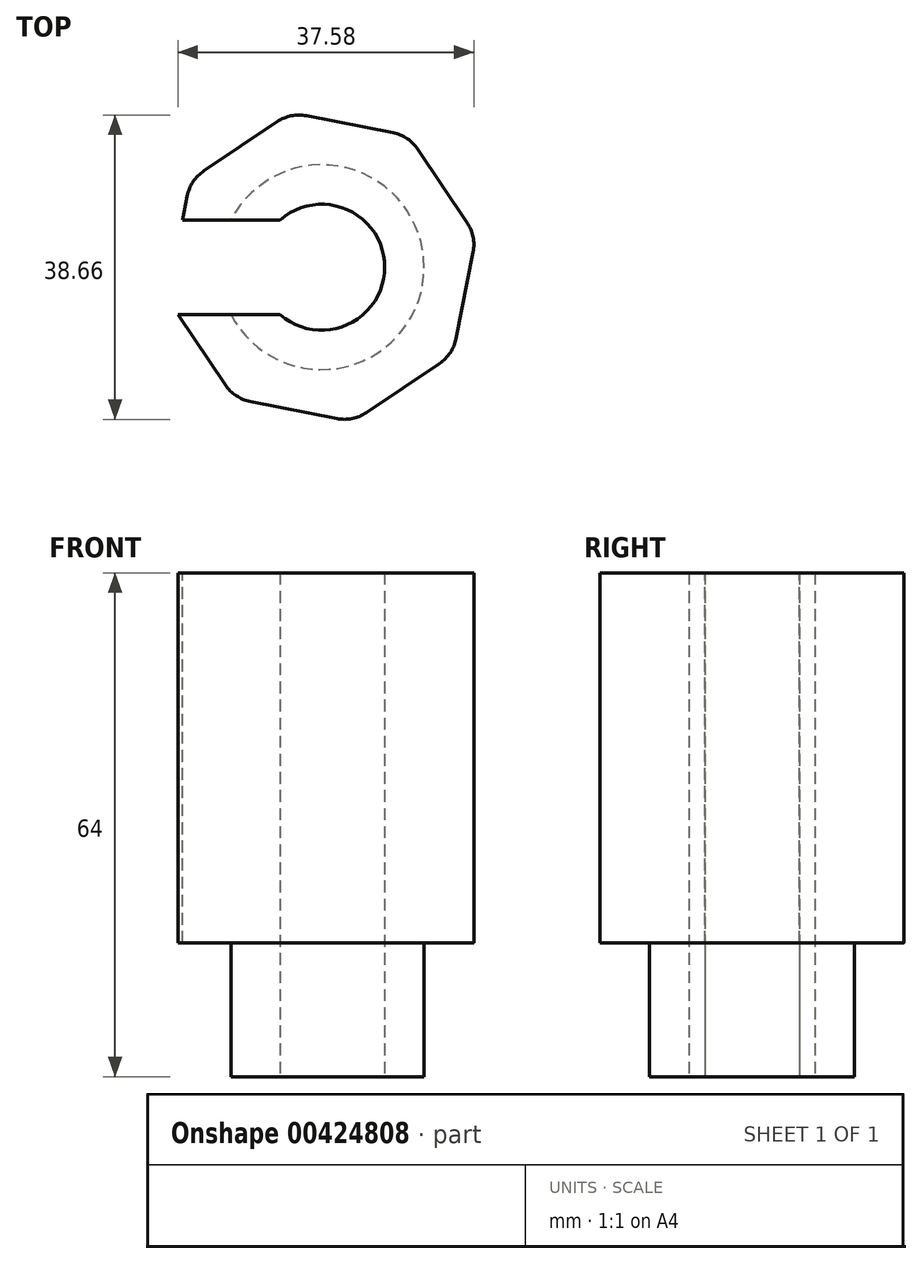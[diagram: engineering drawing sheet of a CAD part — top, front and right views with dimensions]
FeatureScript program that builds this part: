
annotation { "Feature Type Name" : "Feature", "Feature Type Description" : "" }
export const myFeature = defineFeature(function(context is Context, id is Id, definition is map)
    precondition{}
    {
        {
            var Q0;
            Q0=qCreatedBy(makeId("Top.planeOp"),FACE);
            var sketch = newSketch(context, id + "F0", { "sketchPlane" : qUnion([Q0])});
            skCircle(sketch, "E0", {"center": v(0, 0) * mm, "radius": 13 * mm});
            skCircle(sketch, "E1", {"center": v(0, 0) * mm, "radius": 8 * mm});
            skLineSegment(sketch, "E2", {"start": v(-9.15, -9.23) * mm, "end": v(0, 0) * mm});
            skLineSegment(sketch, "E3", {"start": v(0, 0) * mm, "end": v(9.15, 9.23) * mm});
            skLineSegment(sketch, "E4", {"start": v(0, 0) * mm, "end": v(-9.23, 9.15) * mm});
            skLineSegment(sketch, "E5.bottom", {"start": v(-9.15, -9.23) * mm, "end": v(9.15, -9.23) * mm});
            skLineSegment(sketch, "E5.top", {"start": v(-9.15, 9.15) * mm, "end": v(9.15, 9.15) * mm});
            skLineSegment(sketch, "E5.left", {"start": v(-9.15, -9.23) * mm, "end": v(-9.15, 9.15) * mm});
            skLineSegment(sketch, "E5.right", {"start": v(9.15, -9.23) * mm, "end": v(9.15, 9.15) * mm});
            skSolve(sketch);
        }
        {
            var Q0;
            {var subQ0=sQuery(id+"F0.wireOp",EDGE,"E5.bottom");Q0=makeQuery(id+"F0.imprint","IMPRINT",FACE,{"disambiguationData":[TD([[makeQuery(id+"F0.imprint","IMPRINT",EDGE,{"derivedFrom":subQ0}),-1.0]])]});}
            var Q1;
            {var subQ0=sQuery(id+"F0.wireOp",EDGE,"E5.bottom");Q1=makeQuery(id+"F0.imprint","IMPRINT",FACE,{"disambiguationData":[TD([[makeQuery(id+"F0.imprint","IMPRINT",EDGE,{"derivedFrom":subQ0}),1.0]])]});}
            var Q2;
            {var subQ0=sQuery(id+"F0.wireOp",EDGE,"E4");var subQ1=sQuery(id+"F0.wireOp",EDGE,"E1");var subQ2=makeQuery(id+"F0.imprint","INTERSECT",VERTEX,{"derivedFrom":[subQ1,subQ0]});Q2=makeQuery(id+"F0.imprint","IMPRINT",FACE,{"disambiguationData":[TD([[makeQuery(id+"F0.imprint","IMPRINT",EDGE,{"disambiguationData":[TD([[subQ2,-1.0]])],"derivedFrom":subQ1}),-1.0]])]});}
            var Q3;
            {var subQ5=sQuery(id+"F0.wireOp",EDGE,"E4");var subQ6=sQuery(id+"F0.wireOp",EDGE,"E1");var subQ7=makeQuery(id+"F0.imprint","INTERSECT",VERTEX,{"derivedFrom":[subQ6,subQ5]});Q3=makeQuery(id+"F0.imprint","IMPRINT",FACE,{"disambiguationData":[TD([[makeQuery(id+"F0.imprint","IMPRINT",EDGE,{"disambiguationData":[TD([[subQ7,1.0]])],"derivedFrom":subQ6}),-1.0]])]});}
            var Q4;
            {var subQ1=sQuery(id+"F0.wireOp",EDGE,"E0");var subQ7=sQuery(id+"F0.wireOp",EDGE,"E3");var subQ9=makeQuery(id+"F0.imprint","INTERSECT",VERTEX,{"derivedFrom":[subQ1,subQ7]});Q4=makeQuery(id+"F0.imprint","IMPRINT",FACE,{"disambiguationData":[TD([[makeQuery(id+"F0.imprint","IMPRINT",EDGE,{"disambiguationData":[TD([[subQ9,-1.0]])],"derivedFrom":subQ1}),1.0]])]});}
            extrude(context, id + "F1", {"entities" : qUnion([Q0, Q1, Q2, Q3, Q4]), "depth" : 24 * mm});
        }
        {
            var Q0;
            Q0 = qSketchRegion(id + "F0", true);
            var Q1;
            Q1=sQuery(id+"F0.wireOp",EDGE,"E0");
            var Q2;
            Q2=sQuery(id+"F0.wireOp",EDGE,"E1");
            extrude(context, id + "F2", {"entities" : qUnion([Q0]), "operationType" : NewBodyOperationType.ADD, "surfaceEntities" : qUnion([Q1, Q2]), "depth" : 17 * mm});
        }
        {
            var Q0;
            Q0=makeQuery(id+"F1.opExtrude","CAP_FACE",FACE,{"disambiguationData":[OSD([sQuery(id+"F0.wireOp",EDGE,"E0"),sQuery(id+"F0.wireOp",EDGE,"E1"),sQuery(id+"F0.wireOp",EDGE,"E3"),sQuery(id+"F0.wireOp",EDGE,"E4"),sQuery(id+"F0.wireOp",EDGE,"E5.top"),sQuery(id+"F0.wireOp",EDGE,"E5.left"),sQuery(id+"F0.wireOp",EDGE,"E5.right")])],"isStart":false});
            var sketch = newSketch(context, id + "F3", { "sketchPlane" : qUnion([Q0])});
            skLineSegment(sketch, "E6", {"start": v(-9.15, -9.23) * mm, "end": v(-9.15, 9.07) * mm});
            skLineSegment(sketch, "E7", {"start": v(9.15, -9.23) * mm, "end": v(9.15, 9.23) * mm});
            skArc(sketch, "E8", {"start": v(9.15, 9.23) * mm, "mid": v(-0.03, 12.94) * mm, "end": v(-9.15, 9.07) * mm});
            skArc(sketch, "E9", {"start": v(-9.15, -9.23) * mm, "mid": v(0, -13) * mm, "end": v(9.15, -9.23) * mm});
            skSolve(sketch);
        }
        {
            var Q0;
            Q0=makeQuery(id+"F3.imprint","IMPRINT",FACE,{"disambiguationData":[TD([[makeQuery(id+"F3.imprint","IMPRINT",EDGE,{"derivedFrom":sQuery(id+"F3.wireOp",EDGE,"E6")}),-1.0]])]});
            extrude(context, id + "F4", {"entities" : qUnion([Q0]), "depth" : 40 * mm});
        }
        {
            var Q0;
            {var subQ0=sQuery(id+"F0.wireOp",EDGE,"E4");var subQ1=sQuery(id+"F0.wireOp",EDGE,"E5.left");var subQ3=sQuery(id+"F0.wireOp",EDGE,"E0");var subQ4=sQuery(id+"F0.wireOp",EDGE,"E3");Q0=makeQuery(id+"F2.boolean.opBoolean","SPLIT",FACE,{"disambiguationData":[TD([makeQuery(id+"F1.opExtrude","SWEPT_FACE",FACE,{"disambiguationData":[OSD([subQ0])]})])],"derivedFrom":makeQuery(id+"F2.opExtrude","CAP_FACE",FACE,{"disambiguationData":[OSD([subQ3,sQuery(id+"F0.wireOp",EDGE,"E1"),subQ4,subQ0,sQuery(id+"F0.wireOp",EDGE,"E5.top"),subQ1])],"isStart":false})});}
            var sketch = newSketch(context, id + "F5", { "sketchPlane" : qUnion([Q0])});
            skSolve(sketch);
        }
        {
            var Q0;
            Q0 = qSketchRegion(id + "F5", true);
            var Q1;
            {var subQ0=sQuery(id+"F0.wireOp",EDGE,"E5.left");var subQ1=sQuery(id+"F0.wireOp",EDGE,"E4");var subQ2=sQuery(id+"F0.wireOp",EDGE,"E3");var subQ3=sQuery(id+"F0.wireOp",EDGE,"E0");var subQ4=makeQuery(id+"F2.opExtrude","CAP_FACE",FACE,{"disambiguationData":[OSD([subQ3,sQuery(id+"F0.wireOp",EDGE,"E1"),subQ2,subQ1,sQuery(id+"F0.wireOp",EDGE,"E5.top"),subQ0])],"isStart":false});var subQ5=makeQuery(id+"F1.opExtrude","SWEPT_FACE",FACE,{"disambiguationData":[OSD([subQ1])]});Q1=makeQuery(id+"F5.imprint","IMPRINT",FACE,{"disambiguationData":[TD([[makeQuery(id+"F5.imprint","IMPRINT",EDGE,{"derivedFrom":makeQuery(id+"F2.boolean.opBoolean","INTERSECT",EDGE,{"derivedFrom":[subQ5,subQ4]})}),1.0]])]});}
            extrude(context, id + "F6", {"entities" : qUnion([Q0, Q1]), "operationType" : NewBodyOperationType.ADD, "depth" : 47 * mm});
        }
        {
            var Q0;
            {var subQ0=sQuery(id+"F0.wireOp",EDGE,"E5.top");var subQ1=sQuery(id+"F0.wireOp",EDGE,"E5.left");var subQ3=sQuery(id+"F0.wireOp",EDGE,"E0");var subQ5=sQuery(id+"F0.wireOp",EDGE,"E3");var subQ6=sQuery(id+"F0.wireOp",EDGE,"E4");Q0=makeQuery(id+"F2.boolean.opBoolean","SPLIT",FACE,{"disambiguationData":[TD([makeQuery(id+"F1.opExtrude","SWEPT_FACE",FACE,{"disambiguationData":[OSD([subQ5])]})])],"derivedFrom":makeQuery(id+"F2.opExtrude","CAP_FACE",FACE,{"disambiguationData":[OSD([subQ3,sQuery(id+"F0.wireOp",EDGE,"E1"),subQ5,subQ6,subQ0,subQ1])],"isStart":false})});}
            var sketch = newSketch(context, id + "F7", { "sketchPlane" : qUnion([Q0])});
            skSolve(sketch);
        }
        {
            var Q0;
            {var subQ0=sQuery(id+"F0.wireOp",EDGE,"E5.left");var subQ1=sQuery(id+"F0.wireOp",EDGE,"E5.top");var subQ2=sQuery(id+"F0.wireOp",EDGE,"E4");var subQ3=sQuery(id+"F0.wireOp",EDGE,"E3");var subQ4=sQuery(id+"F0.wireOp",EDGE,"E0");var subQ5=makeQuery(id+"F2.opExtrude","CAP_FACE",FACE,{"disambiguationData":[OSD([subQ4,sQuery(id+"F0.wireOp",EDGE,"E1"),subQ3,subQ2,subQ1,subQ0])],"isStart":false});var subQ6=makeQuery(id+"F1.opExtrude","SWEPT_FACE",FACE,{"disambiguationData":[OSD([subQ3])]});Q0=makeQuery(id+"F7.imprint","IMPRINT",FACE,{"disambiguationData":[TD([[makeQuery(id+"F7.imprint","IMPRINT",EDGE,{"derivedFrom":makeQuery(id+"F2.boolean.opBoolean","INTERSECT",EDGE,{"derivedFrom":[subQ6,subQ5]})}),-1.0]])]});}
            extrude(context, id + "F8", {"entities" : qUnion([Q0]), "operationType" : NewBodyOperationType.ADD, "depth" : 47 * mm});
        }
        {
            var Q0;
            {var subQ0=sQuery(id+"F0.wireOp",EDGE,"E5.left");var subQ1=sQuery(id+"F0.wireOp",EDGE,"E5.top");var subQ2=sQuery(id+"F0.wireOp",EDGE,"E4");var subQ3=sQuery(id+"F0.wireOp",EDGE,"E3");var subQ4=sQuery(id+"F0.wireOp",EDGE,"E1");var subQ5=sQuery(id+"F0.wireOp",EDGE,"E0");Q0=makeQuery(id+"F8.boolean.opBoolean","MERGE",FACE,{"derivedFrom":[makeQuery(id+"F6.boolean.opBoolean","MERGE",FACE,{"derivedFrom":[makeQuery(id+"F4.opExtrude","CAP_FACE",FACE,{"disambiguationData":[OSD([subQ4,subQ3,subQ1,sQuery(id+"F3.wireOp",EDGE,"E6"),sQuery(id+"F3.wireOp",EDGE,"E7"),sQuery(id+"F3.wireOp",EDGE,"E8"),sQuery(id+"F3.wireOp",EDGE,"E9")])],"isStart":false}),makeQuery(id+"F6.opExtrude","CAP_FACE",FACE,{"disambiguationData":[OSD([subQ5,subQ4,subQ3,subQ2,subQ1,subQ0])],"isStart":false})]}),makeQuery(id+"F8.opExtrude","CAP_FACE",FACE,{"disambiguationData":[OSD([subQ5,subQ4,subQ3,subQ2,subQ1,subQ0,sQuery(id+"F0.wireOp",EDGE,"E5.right")])],"isStart":false})]});}
            var sketch = newSketch(context, id + "F9", { "sketchPlane" : qUnion([Q0])});
            skCircle(sketch, "E10", {"center": v(0, 0) * mm, "radius": 18.5 * mm});
            skCircle(sketch, "E11.cCircle", {"center": v(0, 0) * mm, "radius": 18.5 * mm, "construction": true});
            skLineSegment(sketch, "E11.0", {"start": v(-11.09, -16.67) * mm, "end": v(-19.63, -3.95) * mm});
            skLineSegment(sketch, "E11.1", {"start": v(-19.63, -3.95) * mm, "end": v(-16.67, 11.09) * mm});
            skLineSegment(sketch, "E11.2", {"start": v(-16.67, 11.09) * mm, "end": v(-3.95, 19.63) * mm});
            skLineSegment(sketch, "E11.3", {"start": v(-3.95, 19.63) * mm, "end": v(11.09, 16.67) * mm});
            skLineSegment(sketch, "E11.4", {"start": v(11.09, 16.67) * mm, "end": v(19.63, 3.95) * mm});
            skLineSegment(sketch, "E11.5", {"start": v(19.63, 3.95) * mm, "end": v(16.67, -11.09) * mm});
            skLineSegment(sketch, "E11.6", {"start": v(16.67, -11.09) * mm, "end": v(3.95, -19.63) * mm});
            skLineSegment(sketch, "E11.7", {"start": v(3.95, -19.63) * mm, "end": v(-11.09, -16.67) * mm});
            skPoint(sketch, "E11.0.midPoint", {"position": v(-15.36, -10.31) * mm});
            skSolve(sketch);
        }
        {
            var Q0;
            Q0=makeQuery(id+"F9.imprint","IMPRINT",FACE,{"disambiguationData":[TD([[makeQuery(id+"F9.imprint","IMPRINT",EDGE,{"derivedFrom":sQuery(id+"F9.wireOp",EDGE,"E10")}),1.0]])]});
            var Q1;
            {var subQ0=sQuery(id+"F9.wireOp",EDGE,"E11.7");var subQ1=sQuery(id+"F9.wireOp",EDGE,"E10");var subQ2=makeQuery(id+"F9.imprint","INTERSECT",VERTEX,{"derivedFrom":[subQ1,subQ0]});Q1=makeQuery(id+"F9.imprint","IMPRINT",FACE,{"disambiguationData":[TD([[makeQuery(id+"F9.imprint","IMPRINT",EDGE,{"disambiguationData":[TD([[subQ2,-1.0]])],"derivedFrom":subQ1}),-1.0]])]});}
            var Q2;
            {var subQ0=sQuery(id+"F9.wireOp",EDGE,"E11.0");var subQ1=sQuery(id+"F9.wireOp",EDGE,"E10");var subQ2=makeQuery(id+"F9.imprint","INTERSECT",VERTEX,{"derivedFrom":[subQ1,subQ0]});Q2=makeQuery(id+"F9.imprint","IMPRINT",FACE,{"disambiguationData":[TD([[makeQuery(id+"F9.imprint","IMPRINT",EDGE,{"disambiguationData":[TD([[subQ2,-1.0]])],"derivedFrom":subQ1}),-1.0]])]});}
            var Q3;
            {var subQ0=sQuery(id+"F9.wireOp",EDGE,"E11.1");var subQ1=sQuery(id+"F9.wireOp",EDGE,"E10");var subQ2=makeQuery(id+"F9.imprint","INTERSECT",VERTEX,{"derivedFrom":[subQ1,subQ0]});Q3=makeQuery(id+"F9.imprint","IMPRINT",FACE,{"disambiguationData":[TD([[makeQuery(id+"F9.imprint","IMPRINT",EDGE,{"disambiguationData":[TD([[subQ2,-1.0]])],"derivedFrom":subQ1}),-1.0]])]});}
            var Q4;
            {var subQ0=sQuery(id+"F9.wireOp",EDGE,"E11.2");var subQ1=sQuery(id+"F9.wireOp",EDGE,"E10");var subQ2=makeQuery(id+"F9.imprint","INTERSECT",VERTEX,{"derivedFrom":[subQ1,subQ0]});Q4=makeQuery(id+"F9.imprint","IMPRINT",FACE,{"disambiguationData":[TD([[makeQuery(id+"F9.imprint","IMPRINT",EDGE,{"disambiguationData":[TD([[subQ2,-1.0]])],"derivedFrom":subQ1}),-1.0]])]});}
            var Q5;
            {var subQ0=sQuery(id+"F9.wireOp",EDGE,"E11.3");var subQ1=sQuery(id+"F9.wireOp",EDGE,"E10");var subQ2=makeQuery(id+"F9.imprint","INTERSECT",VERTEX,{"derivedFrom":[subQ1,subQ0]});Q5=makeQuery(id+"F9.imprint","IMPRINT",FACE,{"disambiguationData":[TD([[makeQuery(id+"F9.imprint","IMPRINT",EDGE,{"disambiguationData":[TD([[subQ2,-1.0]])],"derivedFrom":subQ1}),-1.0]])]});}
            var Q6;
            {var subQ0=sQuery(id+"F9.wireOp",EDGE,"E11.3");var subQ1=sQuery(id+"F9.wireOp",EDGE,"E10");var subQ2=makeQuery(id+"F9.imprint","INTERSECT",VERTEX,{"derivedFrom":[subQ1,subQ0]});Q6=makeQuery(id+"F9.imprint","IMPRINT",FACE,{"disambiguationData":[TD([[makeQuery(id+"F9.imprint","IMPRINT",EDGE,{"disambiguationData":[TD([[subQ2,1.0]])],"derivedFrom":subQ1}),-1.0]])]});}
            var Q7;
            {var subQ0=sQuery(id+"F9.wireOp",EDGE,"E11.4");var subQ1=sQuery(id+"F9.wireOp",EDGE,"E10");var subQ2=makeQuery(id+"F9.imprint","INTERSECT",VERTEX,{"derivedFrom":[subQ1,subQ0]});Q7=makeQuery(id+"F9.imprint","IMPRINT",FACE,{"disambiguationData":[TD([[makeQuery(id+"F9.imprint","IMPRINT",EDGE,{"disambiguationData":[TD([[subQ2,1.0]])],"derivedFrom":subQ1}),-1.0]])]});}
            var Q8;
            {var subQ0=sQuery(id+"F9.wireOp",EDGE,"E11.6");var subQ1=sQuery(id+"F9.wireOp",EDGE,"E10");var subQ2=makeQuery(id+"F9.imprint","INTERSECT",VERTEX,{"derivedFrom":[subQ1,subQ0]});Q8=makeQuery(id+"F9.imprint","IMPRINT",FACE,{"disambiguationData":[TD([[makeQuery(id+"F9.imprint","IMPRINT",EDGE,{"disambiguationData":[TD([[subQ2,-1.0]])],"derivedFrom":subQ1}),-1.0]])]});}
            extrude(context, id + "F10", {"entities" : qUnion([Q0, Q1, Q2, Q3, Q4, Q5, Q6, Q7, Q8]), "operationType" : NewBodyOperationType.ADD, "oppositeDirection" : true, "depth" : 47 * mm});
        }
        {
            var Q0;
            Q0=qCreatedBy(makeId("Right.planeOp"),FACE);
            var sketch = newSketch(context, id + "F11", { "sketchPlane" : qUnion([Q0])});
            skLineSegment(sketch, "E12.bottom", {"start": v(-6, 0) * mm, "end": v(6, 0) * mm});
            skLineSegment(sketch, "E12.top", {"start": v(-6, 90) * mm, "end": v(6, 90) * mm});
            skLineSegment(sketch, "E12.left", {"start": v(-6, 0) * mm, "end": v(-6, 90) * mm});
            skLineSegment(sketch, "E12.right", {"start": v(6, 0) * mm, "end": v(6, 90) * mm});
            skSolve(sketch);
        }
        {
            var Q0;
            Q0=makeQuery(id+"F11.imprint","IMPRINT",FACE,{"disambiguationData":[TD([[makeQuery(id+"F11.imprint","IMPRINT",EDGE,{"derivedFrom":sQuery(id+"F11.wireOp",EDGE,"E12.bottom")}),1.0]])]});
            extrude(context, id + "F12", {"entities" : qUnion([Q0]), "operationType" : NewBodyOperationType.REMOVE, "oppositeDirection" : true, "depth" : 25 * mm});
        }
        {
            var Q0;
            Q0=makeQuery(id+"F10.opExtrude","SWEPT_EDGE",EDGE,{"disambiguationData":[OSD([sQuery(id+"F9.wireOp",EDGE,"E11.5"),sQuery(id+"F9.wireOp",EDGE,"E11.6")])]});
            var Q1;
            Q1=makeQuery(id+"F10.opExtrude","SWEPT_EDGE",EDGE,{"disambiguationData":[OSD([sQuery(id+"F9.wireOp",EDGE,"E11.6"),sQuery(id+"F9.wireOp",EDGE,"E11.7")])]});
            var Q2;
            Q2=makeQuery(id+"F10.opExtrude","SWEPT_EDGE",EDGE,{"disambiguationData":[OSD([sQuery(id+"F9.wireOp",EDGE,"E11.4"),sQuery(id+"F9.wireOp",EDGE,"E11.5")])]});
            var Q3;
            Q3=makeQuery(id+"F10.opExtrude","SWEPT_EDGE",EDGE,{"disambiguationData":[OSD([sQuery(id+"F9.wireOp",EDGE,"E11.3"),sQuery(id+"F9.wireOp",EDGE,"E11.4")])]});
            var Q4;
            Q4=makeQuery(id+"F10.opExtrude","SWEPT_EDGE",EDGE,{"disambiguationData":[OSD([sQuery(id+"F9.wireOp",EDGE,"E11.2"),sQuery(id+"F9.wireOp",EDGE,"E11.3")])]});
            var Q5;
            Q5=makeQuery(id+"F10.opExtrude","SWEPT_EDGE",EDGE,{"disambiguationData":[OSD([sQuery(id+"F9.wireOp",EDGE,"E11.1"),sQuery(id+"F9.wireOp",EDGE,"E11.2")])]});
            var Q6;
            Q6=makeQuery(id+"F10.opExtrude","SWEPT_EDGE",EDGE,{"disambiguationData":[OSD([sQuery(id+"F9.wireOp",EDGE,"E11.0"),sQuery(id+"F9.wireOp",EDGE,"E11.7")])]});
            fillet(context, id + "F13", {"entities" : qUnion([Q0, Q1, Q2, Q3, Q4, Q5, Q6]), "radius" : 5 * mm, "tangentPropagation" : true, "allowEdgeOverflow" : false});
        }
    });
